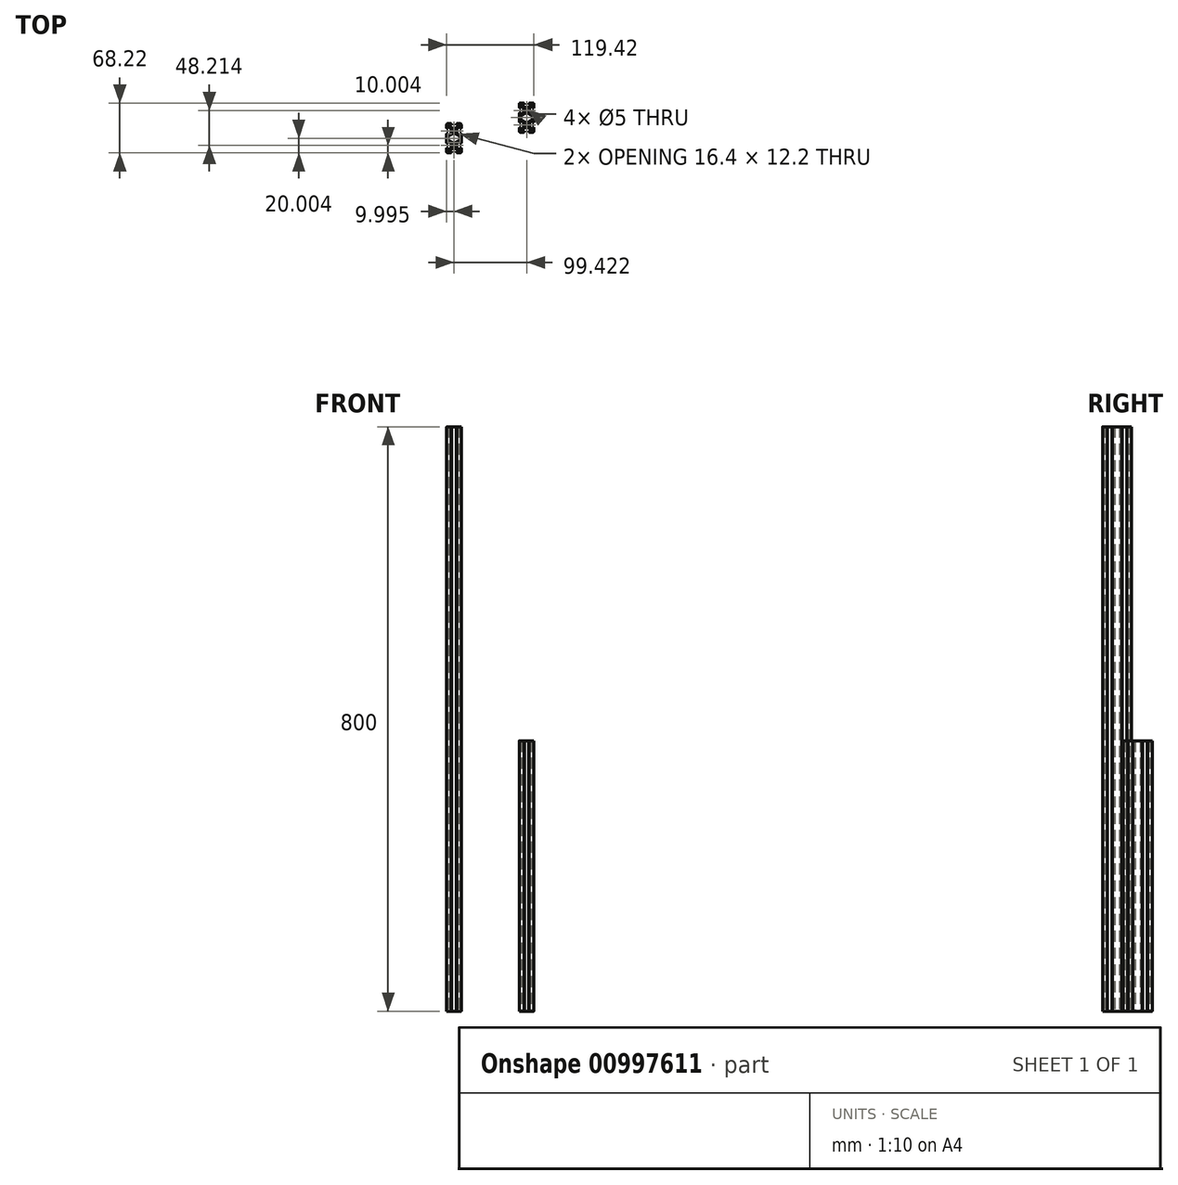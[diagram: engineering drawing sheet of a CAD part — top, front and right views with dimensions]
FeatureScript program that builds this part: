
annotation { "Feature Type Name" : "Feature", "Feature Type Description" : "" }
export const myFeature = defineFeature(function(context is Context, id is Id, definition is map)
    precondition{}
    {
        {
            var Q0;
            Q0=qCreatedBy(makeId("Top.planeOp"),FACE);
            var sketch = newSketch(context, id + "F0", { "sketchPlane" : qUnion([Q0])});
            skCircle(sketch, "E0", {"center": v(-160.4, -45.54) * mm, "radius": 2.5 * mm});
            skLineSegment(sketch, "E1.bottom", {"start": v(-151.9, -55.54) * mm, "end": v(-156.3, -55.54) * mm});
            skLineSegment(sketch, "E1.left", {"start": v(-150.4, -54.04) * mm, "end": v(-150.4, -49.14) * mm});
            skLineSegment(sketch, "E2.bottom", {"start": v(-158.38, -49.44) * mm, "end": v(-162.4, -49.44) * mm});
            skLineSegment(sketch, "E2.top", {"start": v(-158.38, -41.64) * mm, "end": v(-162.4, -41.64) * mm});
            skLineSegment(sketch, "E2.left", {"start": v(-156.5, -47.55) * mm, "end": v(-156.5, -43.52) * mm});
            skLineSegment(sketch, "E2.right", {"start": v(-164.3, -47.55) * mm, "end": v(-164.3, -43.52) * mm});
            skLineSegment(sketch, "E3.left", {"start": v(-150.4, -37.04) * mm, "end": v(-150.4, -40.04) * mm});
            skLineSegment(sketch, "E4", {"start": v(-155.9, -42.11) * mm, "end": v(-153.83, -40.04) * mm});
            skLineSegment(sketch, "E5.MirrorCS", {"start": v(-156.97, -41.05) * mm, "end": v(-154.9, -38.98) * mm});
            skLineSegment(sketch, "E6", {"start": v(-152.2, -40.04) * mm, "end": v(-152.2, -42.44) * mm});
            skLineSegment(sketch, "E7", {"start": v(-150.7, -41.94) * mm, "end": v(-150.4, -41.94) * mm});
            skLineSegment(sketch, "E8", {"start": v(-152.2, -42.44) * mm, "end": v(-150.9, -42.44) * mm});
            skLineSegment(sketch, "E9", {"start": v(-150.9, -42.14) * mm, "end": v(-150.9, -42.44) * mm});
            skPoint(sketch, "E10.visualSharp", {"position": v(-150.9, -41.94) * mm});
            skArc(sketch, "E10.filletArc", {"start": v(-150.7, -41.94) * mm, "mid": v(-150.84, -42) * mm, "end": v(-150.9, -42.14) * mm});
            skPoint(sketch, "E11.newPointA", {"position": v(-156.5, -42.7) * mm});
            skArc(sketch, "E11.filletArc", {"start": v(-155.9, -42.11) * mm, "mid": v(-156.34, -42.76) * mm, "end": v(-156.5, -43.52) * mm});
            skPoint(sketch, "E12.newPointA", {"position": v(-157.56, -41.64) * mm});
            skPoint(sketch, "E12.newPointB", {"position": v(-156.5, -41.64) * mm});
            skArc(sketch, "E12.filletArc", {"start": v(-158.38, -41.64) * mm, "mid": v(-157.62, -41.48) * mm, "end": v(-156.97, -41.05) * mm});
            skLineSegment(sketch, "E13.trimOffspring", {"start": v(-152.2, -40.04) * mm, "end": v(-153.83, -40.04) * mm});
            skLineSegment(sketch, "E14.MirrorCS", {"start": v(-150.7, -49.14) * mm, "end": v(-150.4, -49.14) * mm});
            skArc(sketch, "E15.MirrorCS", {"start": v(-150.7, -49.14) * mm, "mid": v(-150.84, -49.08) * mm, "end": v(-150.9, -48.94) * mm});
            skLineSegment(sketch, "E16.MirrorCS", {"start": v(-150.9, -48.94) * mm, "end": v(-150.9, -48.64) * mm});
            skArc(sketch, "E17.MirrorCS", {"start": v(-155.9, -48.96) * mm, "mid": v(-156.34, -48.31) * mm, "end": v(-156.5, -47.55) * mm});
            skLineSegment(sketch, "E18.MirrorCS", {"start": v(-152.2, -51.04) * mm, "end": v(-153.83, -51.04) * mm});
            skLineSegment(sketch, "E19.MirrorCS", {"start": v(-152.2, -48.64) * mm, "end": v(-150.9, -48.64) * mm});
            skLineSegment(sketch, "E20.MirrorCS", {"start": v(-151.9, -55.54) * mm, "end": v(-154.9, -55.54) * mm});
            skPoint(sketch, "E21.MirrorP", {"position": v(-150.9, -49.14) * mm});
            skLineSegment(sketch, "E22.MirrorCS", {"start": v(-157.3, -53.74) * mm, "end": v(-157.3, -55.04) * mm});
            skLineSegment(sketch, "E23.MirrorCS", {"start": v(-154.9, -53.74) * mm, "end": v(-157.3, -53.74) * mm});
            skLineSegment(sketch, "E24.MirrorCS", {"start": v(-152.2, -51.04) * mm, "end": v(-152.2, -48.64) * mm});
            skLineSegment(sketch, "E25.MirrorCS", {"start": v(-150.4, -54.04) * mm, "end": v(-150.4, -51.04) * mm});
            skLineSegment(sketch, "E26.MirrorCS", {"start": v(-155.9, -48.96) * mm, "end": v(-153.83, -51.04) * mm});
            skPoint(sketch, "E27.MirrorP", {"position": v(-156.5, -48.38) * mm});
            skPoint(sketch, "E28.MirrorP", {"position": v(-150.4, -55.54) * mm});
            skPoint(sketch, "E29.MirrorP", {"position": v(-156.5, -49.44) * mm});
            skLineSegment(sketch, "E30.MirrorCS", {"start": v(-156.97, -50.02) * mm, "end": v(-154.9, -52.1) * mm});
            skPoint(sketch, "E31.MirrorP", {"position": v(-157.56, -49.44) * mm});
            skArc(sketch, "E32.MirrorCS", {"start": v(-150.4, -54.04) * mm, "mid": v(-150.83, -55.1) * mm, "end": v(-151.9, -55.54) * mm});
            skLineSegment(sketch, "E33.MirrorCS", {"start": v(-154.9, -53.74) * mm, "end": v(-154.9, -52.1) * mm});
            skArc(sketch, "E34.MirrorCS", {"start": v(-158.38, -49.44) * mm, "mid": v(-157.62, -49.59) * mm, "end": v(-156.97, -50.02) * mm});
            skLineSegment(sketch, "E35.trimOffspring", {"start": v(-150.4, -41.94) * mm, "end": v(-150.4, -37.04) * mm});
            skLineSegment(sketch, "E36.MirrorCS", {"start": v(-156.8, -55.24) * mm, "end": v(-156.8, -55.54) * mm});
            skLineSegment(sketch, "E37.MirrorCS", {"start": v(-157, -55.04) * mm, "end": v(-157.3, -55.04) * mm});
            skLineSegment(sketch, "E38.MirrorCS", {"start": v(-156.3, -55.54) * mm, "end": v(-156.8, -55.54) * mm});
            skArc(sketch, "E39.MirrorCS", {"start": v(-156.8, -55.24) * mm, "mid": v(-156.85, -55.1) * mm, "end": v(-157, -55.04) * mm});
            skArc(sketch, "E40.MirrorCS", {"start": v(-170.1, -49.14) * mm, "mid": v(-169.95, -49.08) * mm, "end": v(-169.9, -48.94) * mm});
            skLineSegment(sketch, "E41.MirrorCS", {"start": v(-170.1, -41.94) * mm, "end": v(-170.4, -41.94) * mm});
            skLineSegment(sketch, "E42.MirrorCS", {"start": v(-169.9, -48.94) * mm, "end": v(-169.9, -48.64) * mm});
            skArc(sketch, "E43.MirrorCS", {"start": v(-170.1, -41.94) * mm, "mid": v(-169.95, -42) * mm, "end": v(-169.9, -42.14) * mm});
            skLineSegment(sketch, "E44.MirrorCS", {"start": v(-169.9, -42.14) * mm, "end": v(-169.9, -42.44) * mm});
            skLineSegment(sketch, "E45.MirrorCS", {"start": v(-170.1, -49.14) * mm, "end": v(-170.4, -49.14) * mm});
            skArc(sketch, "E46.MirrorCS", {"start": v(-170.4, -54.04) * mm, "mid": v(-169.96, -55.1) * mm, "end": v(-168.9, -55.54) * mm});
            skArc(sketch, "E47.MirrorCS", {"start": v(-164.88, -42.11) * mm, "mid": v(-164.45, -42.76) * mm, "end": v(-164.3, -43.52) * mm});
            skLineSegment(sketch, "E48.MirrorCS", {"start": v(-163.8, -55.04) * mm, "end": v(-163.5, -55.04) * mm});
            skLineSegment(sketch, "E49.MirrorCS", {"start": v(-162.4, -41.64) * mm, "end": v(-158.38, -41.64) * mm});
            skLineSegment(sketch, "E50.MirrorCS", {"start": v(-168.6, -48.64) * mm, "end": v(-169.9, -48.64) * mm});
            skLineSegment(sketch, "E51.MirrorCS", {"start": v(-168.6, -42.44) * mm, "end": v(-169.9, -42.44) * mm});
            skArc(sketch, "E52.MirrorCS", {"start": v(-164.88, -48.96) * mm, "mid": v(-164.45, -48.31) * mm, "end": v(-164.3, -47.55) * mm});
            skArc(sketch, "E53.MirrorCS", {"start": v(-164, -55.24) * mm, "mid": v(-163.94, -55.1) * mm, "end": v(-163.8, -55.04) * mm});
            skLineSegment(sketch, "E54.MirrorCS", {"start": v(-164, -55.24) * mm, "end": v(-164, -55.54) * mm});
            skLineSegment(sketch, "E55.MirrorCS", {"start": v(-162.4, -49.44) * mm, "end": v(-158.38, -49.44) * mm});
            skLineSegment(sketch, "E56.MirrorCS", {"start": v(-164.5, -55.54) * mm, "end": v(-164, -55.54) * mm});
            skLineSegment(sketch, "E57.MirrorCS", {"start": v(-163.5, -53.74) * mm, "end": v(-163.5, -55.04) * mm});
            skArc(sketch, "E58.MirrorCS", {"start": v(-162.4, -41.64) * mm, "mid": v(-163.17, -41.48) * mm, "end": v(-163.82, -41.05) * mm});
            skPoint(sketch, "E59.MirrorP", {"position": v(-170.4, -55.54) * mm});
            skLineSegment(sketch, "E60.MirrorCS", {"start": v(-168.9, -55.54) * mm, "end": v(-164.5, -55.54) * mm});
            skPoint(sketch, "E61.MirrorP", {"position": v(-164.3, -49.44) * mm});
            skArc(sketch, "E62.MirrorCS", {"start": v(-162.4, -49.44) * mm, "mid": v(-163.17, -49.59) * mm, "end": v(-163.82, -50.02) * mm});
            skPoint(sketch, "E63.MirrorP", {"position": v(-164.3, -48.38) * mm});
            skLineSegment(sketch, "E64.MirrorCS", {"start": v(-163.82, -41.05) * mm, "end": v(-165.9, -38.98) * mm});
            skPoint(sketch, "E65.MirrorP", {"position": v(-164.3, -42.7) * mm});
            skLineSegment(sketch, "E66.MirrorCS", {"start": v(-168.6, -51.04) * mm, "end": v(-168.6, -48.64) * mm});
            skLineSegment(sketch, "E67.MirrorCS", {"start": v(-164.88, -48.96) * mm, "end": v(-166.96, -51.04) * mm});
            skLineSegment(sketch, "E68.MirrorCS", {"start": v(-165.9, -53.74) * mm, "end": v(-163.5, -53.74) * mm});
            skLineSegment(sketch, "E69.MirrorCS", {"start": v(-168.6, -51.04) * mm, "end": v(-166.96, -51.04) * mm});
            skLineSegment(sketch, "E70.MirrorCS", {"start": v(-170.4, -54.04) * mm, "end": v(-170.4, -51.04) * mm});
            skLineSegment(sketch, "E71.MirrorCS", {"start": v(-170.4, -41.94) * mm, "end": v(-170.4, -37.04) * mm});
            skLineSegment(sketch, "E72.MirrorCS", {"start": v(-163.82, -50.02) * mm, "end": v(-165.9, -52.1) * mm});
            skPoint(sketch, "E73.MirrorP", {"position": v(-163.23, -49.44) * mm});
            skLineSegment(sketch, "E74.MirrorCS", {"start": v(-168.6, -40.04) * mm, "end": v(-168.6, -42.44) * mm});
            skLineSegment(sketch, "E75.MirrorCS", {"start": v(-170.4, -37.04) * mm, "end": v(-170.4, -40.04) * mm});
            skPoint(sketch, "E76.MirrorP", {"position": v(-169.9, -49.14) * mm});
            skPoint(sketch, "E77.MirrorP", {"position": v(-170.4, -35.54) * mm});
            skPoint(sketch, "E78.MirrorP", {"position": v(-169.9, -41.94) * mm});
            skLineSegment(sketch, "E79.MirrorCS", {"start": v(-164.88, -42.11) * mm, "end": v(-166.96, -40.04) * mm});
            skLineSegment(sketch, "E80.MirrorCS", {"start": v(-168.6, -40.04) * mm, "end": v(-166.96, -40.04) * mm});
            skLineSegment(sketch, "E81.MirrorCS", {"start": v(-170.4, -54.04) * mm, "end": v(-170.4, -49.14) * mm});
            skLineSegment(sketch, "E82.MirrorCS", {"start": v(-168.9, -55.54) * mm, "end": v(-165.9, -55.54) * mm});
            skPoint(sketch, "E83.MirrorP", {"position": v(-164.3, -41.64) * mm});
            skPoint(sketch, "E84.MirrorP", {"position": v(-163.23, -41.64) * mm});
            skLineSegment(sketch, "E85.MirrorCS", {"start": v(-165.9, -53.74) * mm, "end": v(-165.9, -52.1) * mm});
            skLineSegment(sketch, "E86", {"start": v(-168.6, -38.98) * mm, "end": v(-168.6, -35.54) * mm});
            skLineSegment(sketch, "E87", {"start": v(-170.4, -37.04) * mm, "end": v(-170.4, -35.54) * mm});
            skLineSegment(sketch, "E88", {"start": v(-150.4, -35.54) * mm, "end": v(-150.4, -37.04) * mm});
            skLineSegment(sketch, "E89", {"start": v(-152.2, -38.98) * mm, "end": v(-152.2, -35.54) * mm});
            skLineSegment(sketch, "E90", {"start": v(-154.9, -38.98) * mm, "end": v(-152.2, -38.98) * mm});
            skLineSegment(sketch, "E91", {"start": v(-165.9, -38.98) * mm, "end": v(-168.6, -38.98) * mm});
            skLineSegment(sketch, "E92.MirrorCS", {"start": v(-150.7, -21.94) * mm, "end": v(-150.4, -21.94) * mm});
            skLineSegment(sketch, "E93.MirrorCS", {"start": v(-150.9, -22.14) * mm, "end": v(-150.9, -22.44) * mm});
            skArc(sketch, "E94.MirrorCS", {"start": v(-150.7, -21.94) * mm, "mid": v(-150.84, -22) * mm, "end": v(-150.9, -22.14) * mm});
            skArc(sketch, "E95.MirrorCS", {"start": v(-150.7, -29.14) * mm, "mid": v(-150.84, -29.08) * mm, "end": v(-150.9, -28.94) * mm});
            skLineSegment(sketch, "E96.MirrorCS", {"start": v(-150.9, -28.94) * mm, "end": v(-150.9, -28.64) * mm});
            skLineSegment(sketch, "E97.MirrorCS", {"start": v(-169.9, -22.14) * mm, "end": v(-169.9, -22.44) * mm});
            skLineSegment(sketch, "E98.MirrorCS", {"start": v(-150.7, -29.14) * mm, "end": v(-150.4, -29.14) * mm});
            skArc(sketch, "E99.MirrorCS", {"start": v(-170.1, -21.94) * mm, "mid": v(-169.95, -22) * mm, "end": v(-169.9, -22.14) * mm});
            skLineSegment(sketch, "E100.MirrorCS", {"start": v(-170.1, -21.94) * mm, "end": v(-170.4, -21.94) * mm});
            skLineSegment(sketch, "E101.MirrorCS", {"start": v(-169.9, -28.94) * mm, "end": v(-169.9, -28.64) * mm});
            skArc(sketch, "E102.MirrorCS", {"start": v(-170.1, -29.14) * mm, "mid": v(-169.95, -29.08) * mm, "end": v(-169.9, -28.94) * mm});
            skLineSegment(sketch, "E103.MirrorCS", {"start": v(-170.1, -29.14) * mm, "end": v(-170.4, -29.14) * mm});
            skArc(sketch, "E104.MirrorCS", {"start": v(-158.38, -21.64) * mm, "mid": v(-157.62, -21.48) * mm, "end": v(-156.97, -21.05) * mm});
            skLineSegment(sketch, "E105.MirrorCS", {"start": v(-156.8, -15.84) * mm, "end": v(-156.8, -15.54) * mm});
            skArc(sketch, "E106.MirrorCS", {"start": v(-158.38, -29.44) * mm, "mid": v(-157.62, -29.59) * mm, "end": v(-156.97, -30.02) * mm});
            skLineSegment(sketch, "E107.MirrorCS", {"start": v(-152.2, -31.04) * mm, "end": v(-153.83, -31.04) * mm});
            skLineSegment(sketch, "E108.MirrorCS", {"start": v(-163.8, -16.04) * mm, "end": v(-163.5, -16.04) * mm});
            skLineSegment(sketch, "E109.MirrorCS", {"start": v(-168.6, -20.04) * mm, "end": v(-166.96, -20.04) * mm});
            skArc(sketch, "E110.MirrorCS", {"start": v(-170.4, -17.04) * mm, "mid": v(-169.96, -15.98) * mm, "end": v(-168.9, -15.54) * mm});
            skLineSegment(sketch, "E111.MirrorCS", {"start": v(-152.2, -28.64) * mm, "end": v(-150.9, -28.64) * mm});
            skLineSegment(sketch, "E112.MirrorCS", {"start": v(-164.5, -15.54) * mm, "end": v(-164, -15.54) * mm});
            skArc(sketch, "E113.MirrorCS", {"start": v(-164.88, -22.11) * mm, "mid": v(-164.45, -22.76) * mm, "end": v(-164.3, -23.52) * mm});
            skArc(sketch, "E114.MirrorCS", {"start": v(-150.4, -17.04) * mm, "mid": v(-150.83, -15.98) * mm, "end": v(-151.9, -15.54) * mm});
            skArc(sketch, "E115.MirrorCS", {"start": v(-162.4, -29.44) * mm, "mid": v(-163.17, -29.59) * mm, "end": v(-163.82, -30.02) * mm});
            skLineSegment(sketch, "E116.MirrorCS", {"start": v(-168.6, -22.44) * mm, "end": v(-169.9, -22.44) * mm});
            skLineSegment(sketch, "E117.MirrorCS", {"start": v(-164, -15.84) * mm, "end": v(-164, -15.54) * mm});
            skLineSegment(sketch, "E118.MirrorCS", {"start": v(-157.3, -17.34) * mm, "end": v(-157.3, -16.04) * mm});
            skLineSegment(sketch, "E119.MirrorCS", {"start": v(-156.3, -15.54) * mm, "end": v(-156.8, -15.54) * mm});
            skLineSegment(sketch, "E120.MirrorCS", {"start": v(-163.5, -17.34) * mm, "end": v(-163.5, -16.04) * mm});
            skArc(sketch, "E121.MirrorCS", {"start": v(-155.9, -28.96) * mm, "mid": v(-156.34, -28.31) * mm, "end": v(-156.5, -27.55) * mm});
            skArc(sketch, "E122.MirrorCS", {"start": v(-164.88, -28.96) * mm, "mid": v(-164.45, -28.31) * mm, "end": v(-164.3, -27.55) * mm});
            skLineSegment(sketch, "E123.MirrorCS", {"start": v(-152.2, -22.44) * mm, "end": v(-150.9, -22.44) * mm});
            skLineSegment(sketch, "E124.MirrorCS", {"start": v(-152.2, -20.04) * mm, "end": v(-153.83, -20.04) * mm});
            skArc(sketch, "E125.MirrorCS", {"start": v(-164, -15.84) * mm, "mid": v(-163.94, -15.98) * mm, "end": v(-163.8, -16.04) * mm});
            skLineSegment(sketch, "E126.MirrorCS", {"start": v(-157, -16.04) * mm, "end": v(-157.3, -16.04) * mm});
            skLineSegment(sketch, "E127.MirrorCS", {"start": v(-168.6, -31.04) * mm, "end": v(-166.96, -31.04) * mm});
            skLineSegment(sketch, "E128.MirrorCS", {"start": v(-168.6, -28.64) * mm, "end": v(-169.9, -28.64) * mm});
            skLineSegment(sketch, "E129.MirrorCS", {"start": v(-154.9, -17.34) * mm, "end": v(-154.9, -18.98) * mm});
            skLineSegment(sketch, "E130.MirrorCS", {"start": v(-165.9, -17.34) * mm, "end": v(-165.9, -18.98) * mm});
            skArc(sketch, "E131.MirrorCS", {"start": v(-162.4, -21.64) * mm, "mid": v(-163.17, -21.48) * mm, "end": v(-163.82, -21.05) * mm});
            skArc(sketch, "E132.MirrorCS", {"start": v(-155.9, -22.11) * mm, "mid": v(-156.34, -22.76) * mm, "end": v(-156.5, -23.52) * mm});
            skArc(sketch, "E133.MirrorCS", {"start": v(-156.8, -15.84) * mm, "mid": v(-156.85, -15.98) * mm, "end": v(-157, -16.04) * mm});
            skPoint(sketch, "E134.MirrorP", {"position": v(-160.4, -25.54) * mm});
            skLineSegment(sketch, "E135.MirrorCS", {"start": v(-164.3, -23.52) * mm, "end": v(-164.3, -27.55) * mm});
            skPoint(sketch, "E136.MirrorP", {"position": v(-164.3, -21.64) * mm});
            skLineSegment(sketch, "E137.MirrorCS", {"start": v(-151.9, -15.54) * mm, "end": v(-154.9, -15.54) * mm});
            skLineSegment(sketch, "E138.MirrorCS", {"start": v(-158.38, -29.44) * mm, "end": v(-162.4, -29.44) * mm});
            skLineSegment(sketch, "E139.MirrorCS", {"start": v(-170.4, -17.04) * mm, "end": v(-170.4, -21.94) * mm});
            skLineSegment(sketch, "E140.MirrorCS", {"start": v(-150.4, -34.04) * mm, "end": v(-150.4, -31.04) * mm});
            skPoint(sketch, "E141.MirrorP", {"position": v(-156.5, -21.64) * mm});
            skLineSegment(sketch, "E142.MirrorCS", {"start": v(-168.9, -15.54) * mm, "end": v(-164.5, -15.54) * mm});
            skLineSegment(sketch, "E143.MirrorCS", {"start": v(-150.4, -17.04) * mm, "end": v(-150.4, -20.04) * mm});
            skLineSegment(sketch, "E144.MirrorCS", {"start": v(-158.38, -21.64) * mm, "end": v(-162.4, -21.64) * mm});
            skPoint(sketch, "E145.MirrorP", {"position": v(-170.4, -15.54) * mm});
            skLineSegment(sketch, "E146.MirrorCS", {"start": v(-170.4, -34.04) * mm, "end": v(-170.4, -31.04) * mm});
            skCircle(sketch, "E147.MirrorC", {"center": v(-160.4, -25.54) * mm, "radius": 2.5 * mm});
            skPoint(sketch, "E148.MirrorP", {"position": v(-150.4, -15.54) * mm});
            skPoint(sketch, "E149.MirrorP", {"position": v(-169.9, -21.94) * mm});
            skLineSegment(sketch, "E150.MirrorCS", {"start": v(-152.2, -20.04) * mm, "end": v(-152.2, -22.44) * mm});
            skPoint(sketch, "E151.MirrorP", {"position": v(-169.9, -29.14) * mm});
            skPoint(sketch, "E152.MirrorP", {"position": v(-157.56, -21.64) * mm});
            skLineSegment(sketch, "E153.MirrorCS", {"start": v(-163.82, -21.05) * mm, "end": v(-165.9, -18.98) * mm});
            skLineSegment(sketch, "E154.MirrorCS", {"start": v(-165.9, -17.34) * mm, "end": v(-163.5, -17.34) * mm});
            skPoint(sketch, "E155.MirrorP", {"position": v(-156.5, -28.38) * mm});
            skLineSegment(sketch, "E156.MirrorCS", {"start": v(-170.4, -17.04) * mm, "end": v(-170.4, -20.04) * mm});
            skPoint(sketch, "E157.MirrorP", {"position": v(-150.9, -29.14) * mm});
            skLineSegment(sketch, "E158.MirrorCS", {"start": v(-154.9, -32.1) * mm, "end": v(-152.2, -32.1) * mm});
            skLineSegment(sketch, "E159.MirrorCS", {"start": v(-155.9, -22.11) * mm, "end": v(-153.83, -20.04) * mm});
            skLineSegment(sketch, "E160.MirrorCS", {"start": v(-165.9, -32.1) * mm, "end": v(-168.6, -32.1) * mm});
            skLineSegment(sketch, "E161.MirrorCS", {"start": v(-154.9, -17.34) * mm, "end": v(-157.3, -17.34) * mm});
            skLineSegment(sketch, "E162.MirrorCS", {"start": v(-168.6, -20.04) * mm, "end": v(-168.6, -22.44) * mm});
            skPoint(sketch, "E163.MirrorP", {"position": v(-164.3, -22.7) * mm});
            skPoint(sketch, "E164.MirrorP", {"position": v(-156.5, -29.44) * mm});
            skLineSegment(sketch, "E165.MirrorCS", {"start": v(-162.4, -21.64) * mm, "end": v(-158.38, -21.64) * mm});
            skLineSegment(sketch, "E166.MirrorCS", {"start": v(-168.9, -15.54) * mm, "end": v(-165.9, -15.54) * mm});
            skPoint(sketch, "E167.MirrorP", {"position": v(-163.23, -29.44) * mm});
            skLineSegment(sketch, "E168.MirrorCS", {"start": v(-162.4, -29.44) * mm, "end": v(-158.38, -29.44) * mm});
            skPoint(sketch, "E169.MirrorP", {"position": v(-164.3, -28.38) * mm});
            skLineSegment(sketch, "E170.MirrorCS", {"start": v(-150.4, -17.04) * mm, "end": v(-150.4, -21.94) * mm});
            skPoint(sketch, "E171.MirrorP", {"position": v(-156.5, -22.7) * mm});
            skLineSegment(sketch, "E172.MirrorCS", {"start": v(-164.88, -22.11) * mm, "end": v(-166.96, -20.04) * mm});
            skPoint(sketch, "E173.MirrorP", {"position": v(-163.23, -21.64) * mm});
            skLineSegment(sketch, "E174.MirrorCS", {"start": v(-155.9, -28.96) * mm, "end": v(-153.83, -31.04) * mm});
            skLineSegment(sketch, "E175.MirrorCS", {"start": v(-156.97, -21.05) * mm, "end": v(-154.9, -18.98) * mm});
            skLineSegment(sketch, "E176.MirrorCS", {"start": v(-170.4, -29.14) * mm, "end": v(-170.4, -34.04) * mm});
            skPoint(sketch, "E177.MirrorP", {"position": v(-164.3, -29.44) * mm});
            skLineSegment(sketch, "E178.MirrorCS", {"start": v(-156.97, -30.02) * mm, "end": v(-154.9, -32.1) * mm});
            skLineSegment(sketch, "E179.MirrorCS", {"start": v(-168.6, -31.04) * mm, "end": v(-168.6, -28.64) * mm});
            skPoint(sketch, "E180.MirrorP", {"position": v(-157.56, -29.44) * mm});
            skLineSegment(sketch, "E181.MirrorCS", {"start": v(-163.82, -30.02) * mm, "end": v(-165.9, -32.1) * mm});
            skLineSegment(sketch, "E182.MirrorCS", {"start": v(-152.2, -31.04) * mm, "end": v(-152.2, -28.64) * mm});
            skPoint(sketch, "E183.MirrorP", {"position": v(-150.9, -21.94) * mm});
            skLineSegment(sketch, "E184.MirrorCS", {"start": v(-150.4, -29.14) * mm, "end": v(-150.4, -34.04) * mm});
            skLineSegment(sketch, "E185.MirrorCS", {"start": v(-164.88, -28.96) * mm, "end": v(-166.96, -31.04) * mm});
            skLineSegment(sketch, "E186.MirrorCS", {"start": v(-156.5, -23.52) * mm, "end": v(-156.5, -27.55) * mm});
            skLineSegment(sketch, "E187.MirrorCS", {"start": v(-151.9, -15.54) * mm, "end": v(-156.3, -15.54) * mm});
            skLineSegment(sketch, "E188.MirrorCS", {"start": v(-152.2, -32.1) * mm, "end": v(-152.2, -35.54) * mm});
            skLineSegment(sketch, "E189.MirrorCS", {"start": v(-150.4, -35.54) * mm, "end": v(-150.4, -34.04) * mm});
            skLineSegment(sketch, "E190.MirrorCS", {"start": v(-168.6, -32.1) * mm, "end": v(-168.6, -35.54) * mm});
            skLineSegment(sketch, "E191.MirrorCS", {"start": v(-170.4, -34.04) * mm, "end": v(-170.4, -35.54) * mm});
            skSolve(sketch);
        }
        {
            var Q0;
            Q0=makeQuery(id+"F0.imprint","IMPRINT",FACE,{"disambiguationData":[TD([[makeQuery(id+"F0.imprint","IMPRINT",EDGE,{"derivedFrom":sQuery(id+"F0.wireOp",EDGE,"E1.bottom")}),-1.0]])]});
            extrude(context, id + "F1", {"entities" : qUnion([Q0]), "depth" : 800 * mm, "offsetDistance" : 25 * mm});
        }
        {
            var Q0;
            Q0=qCreatedBy(makeId("Top.planeOp"),FACE);
            var sketch = newSketch(context, id + "F2", { "sketchPlane" : qUnion([Q0])});
            skCircle(sketch, "E192", {"center": v(-60.97, -17.32) * mm, "radius": 2.5 * mm});
            skLineSegment(sketch, "E193.bottom", {"start": v(-52.47, -27.32) * mm, "end": v(-56.87, -27.32) * mm});
            skLineSegment(sketch, "E193.left", {"start": v(-50.97, -25.82) * mm, "end": v(-50.97, -20.92) * mm});
            skLineSegment(sketch, "E194.bottom", {"start": v(-58.96, -21.22) * mm, "end": v(-62.98, -21.22) * mm});
            skLineSegment(sketch, "E194.top", {"start": v(-58.96, -13.42) * mm, "end": v(-62.98, -13.42) * mm});
            skLineSegment(sketch, "E194.left", {"start": v(-57.07, -19.33) * mm, "end": v(-57.07, -15.31) * mm});
            skLineSegment(sketch, "E194.right", {"start": v(-64.87, -19.33) * mm, "end": v(-64.87, -15.31) * mm});
            skLineSegment(sketch, "E195.left", {"start": v(-50.97, -8.82) * mm, "end": v(-50.97, -11.82) * mm});
            skLineSegment(sketch, "E196", {"start": v(-56.49, -13.9) * mm, "end": v(-54.41, -11.82) * mm});
            skLineSegment(sketch, "E197.MirrorCS", {"start": v(-57.55, -12.84) * mm, "end": v(-55.47, -10.76) * mm});
            skLineSegment(sketch, "E198", {"start": v(-52.77, -11.82) * mm, "end": v(-52.77, -14.22) * mm});
            skLineSegment(sketch, "E199", {"start": v(-51.27, -13.72) * mm, "end": v(-50.97, -13.72) * mm});
            skLineSegment(sketch, "E200", {"start": v(-52.77, -14.22) * mm, "end": v(-51.47, -14.22) * mm});
            skLineSegment(sketch, "E201", {"start": v(-51.47, -13.92) * mm, "end": v(-51.47, -14.22) * mm});
            skPoint(sketch, "E202.visualSharp", {"position": v(-51.47, -13.72) * mm});
            skArc(sketch, "E202.filletArc", {"start": v(-51.27, -13.72) * mm, "mid": v(-51.41, -13.78) * mm, "end": v(-51.47, -13.92) * mm});
            skPoint(sketch, "E203.newPointA", {"position": v(-57.07, -14.48) * mm});
            skArc(sketch, "E203.filletArc", {"start": v(-56.49, -13.9) * mm, "mid": v(-56.92, -14.55) * mm, "end": v(-57.07, -15.31) * mm});
            skPoint(sketch, "E204.newPointA", {"position": v(-58.13, -13.42) * mm});
            skPoint(sketch, "E204.newPointB", {"position": v(-57.07, -13.42) * mm});
            skArc(sketch, "E204.filletArc", {"start": v(-58.96, -13.42) * mm, "mid": v(-58.2, -13.27) * mm, "end": v(-57.55, -12.84) * mm});
            skLineSegment(sketch, "E205.trimOffspring", {"start": v(-52.77, -11.82) * mm, "end": v(-54.41, -11.82) * mm});
            skLineSegment(sketch, "E206.MirrorCS", {"start": v(-51.27, -20.92) * mm, "end": v(-50.97, -20.92) * mm});
            skArc(sketch, "E207.MirrorCS", {"start": v(-51.27, -20.92) * mm, "mid": v(-51.41, -20.86) * mm, "end": v(-51.47, -20.72) * mm});
            skLineSegment(sketch, "E208.MirrorCS", {"start": v(-51.47, -20.72) * mm, "end": v(-51.47, -20.42) * mm});
            skArc(sketch, "E209.MirrorCS", {"start": v(-56.49, -20.75) * mm, "mid": v(-56.92, -20.1) * mm, "end": v(-57.07, -19.33) * mm});
            skLineSegment(sketch, "E210.MirrorCS", {"start": v(-52.77, -22.82) * mm, "end": v(-54.41, -22.82) * mm});
            skLineSegment(sketch, "E211.MirrorCS", {"start": v(-52.77, -20.42) * mm, "end": v(-51.47, -20.42) * mm});
            skLineSegment(sketch, "E212.MirrorCS", {"start": v(-52.47, -27.32) * mm, "end": v(-55.47, -27.32) * mm});
            skPoint(sketch, "E213.MirrorP", {"position": v(-51.47, -20.92) * mm});
            skLineSegment(sketch, "E214.MirrorCS", {"start": v(-57.87, -25.52) * mm, "end": v(-57.87, -26.82) * mm});
            skLineSegment(sketch, "E215.MirrorCS", {"start": v(-55.47, -25.52) * mm, "end": v(-57.87, -25.52) * mm});
            skLineSegment(sketch, "E216.MirrorCS", {"start": v(-52.77, -22.82) * mm, "end": v(-52.77, -20.42) * mm});
            skLineSegment(sketch, "E217.MirrorCS", {"start": v(-50.97, -25.82) * mm, "end": v(-50.97, -22.82) * mm});
            skLineSegment(sketch, "E218.MirrorCS", {"start": v(-56.49, -20.75) * mm, "end": v(-54.41, -22.82) * mm});
            skPoint(sketch, "E219.MirrorP", {"position": v(-57.07, -20.16) * mm});
            skPoint(sketch, "E220.MirrorP", {"position": v(-50.97, -27.32) * mm});
            skPoint(sketch, "E221.MirrorP", {"position": v(-57.07, -21.22) * mm});
            skLineSegment(sketch, "E222.MirrorCS", {"start": v(-57.55, -21.8) * mm, "end": v(-55.47, -23.88) * mm});
            skPoint(sketch, "E223.MirrorP", {"position": v(-58.13, -21.22) * mm});
            skArc(sketch, "E224.MirrorCS", {"start": v(-50.97, -25.82) * mm, "mid": v(-51.41, -26.88) * mm, "end": v(-52.47, -27.32) * mm});
            skLineSegment(sketch, "E225.MirrorCS", {"start": v(-55.47, -25.52) * mm, "end": v(-55.47, -23.88) * mm});
            skArc(sketch, "E226.MirrorCS", {"start": v(-58.96, -21.22) * mm, "mid": v(-58.2, -21.37) * mm, "end": v(-57.55, -21.8) * mm});
            skLineSegment(sketch, "E227.trimOffspring", {"start": v(-50.97, -13.72) * mm, "end": v(-50.97, -8.82) * mm});
            skLineSegment(sketch, "E228.MirrorCS", {"start": v(-57.37, -27.02) * mm, "end": v(-57.37, -27.32) * mm});
            skLineSegment(sketch, "E229.MirrorCS", {"start": v(-57.57, -26.82) * mm, "end": v(-57.87, -26.82) * mm});
            skLineSegment(sketch, "E230.MirrorCS", {"start": v(-56.87, -27.32) * mm, "end": v(-57.37, -27.32) * mm});
            skArc(sketch, "E231.MirrorCS", {"start": v(-57.37, -27.02) * mm, "mid": v(-57.43, -26.88) * mm, "end": v(-57.57, -26.82) * mm});
            skArc(sketch, "E232.MirrorCS", {"start": v(-70.67, -20.92) * mm, "mid": v(-70.53, -20.86) * mm, "end": v(-70.47, -20.72) * mm});
            skLineSegment(sketch, "E233.MirrorCS", {"start": v(-70.67, -13.72) * mm, "end": v(-70.97, -13.72) * mm});
            skLineSegment(sketch, "E234.MirrorCS", {"start": v(-70.47, -20.72) * mm, "end": v(-70.47, -20.42) * mm});
            skArc(sketch, "E235.MirrorCS", {"start": v(-70.67, -13.72) * mm, "mid": v(-70.53, -13.78) * mm, "end": v(-70.47, -13.92) * mm});
            skLineSegment(sketch, "E236.MirrorCS", {"start": v(-70.47, -13.92) * mm, "end": v(-70.47, -14.22) * mm});
            skLineSegment(sketch, "E237.MirrorCS", {"start": v(-70.67, -20.92) * mm, "end": v(-70.97, -20.92) * mm});
            skArc(sketch, "E238.MirrorCS", {"start": v(-70.97, -25.82) * mm, "mid": v(-70.53, -26.88) * mm, "end": v(-69.47, -27.32) * mm});
            skArc(sketch, "E239.MirrorCS", {"start": v(-65.46, -13.9) * mm, "mid": v(-65.02, -14.55) * mm, "end": v(-64.87, -15.31) * mm});
            skLineSegment(sketch, "E240.MirrorCS", {"start": v(-64.37, -26.82) * mm, "end": v(-64.07, -26.82) * mm});
            skLineSegment(sketch, "E241.MirrorCS", {"start": v(-62.98, -13.42) * mm, "end": v(-58.96, -13.42) * mm});
            skLineSegment(sketch, "E242.MirrorCS", {"start": v(-69.17, -20.42) * mm, "end": v(-70.47, -20.42) * mm});
            skLineSegment(sketch, "E243.MirrorCS", {"start": v(-69.17, -14.22) * mm, "end": v(-70.47, -14.22) * mm});
            skArc(sketch, "E244.MirrorCS", {"start": v(-65.46, -20.75) * mm, "mid": v(-65.02, -20.1) * mm, "end": v(-64.87, -19.33) * mm});
            skArc(sketch, "E245.MirrorCS", {"start": v(-64.57, -27.02) * mm, "mid": v(-64.51, -26.88) * mm, "end": v(-64.37, -26.82) * mm});
            skLineSegment(sketch, "E246.MirrorCS", {"start": v(-64.57, -27.02) * mm, "end": v(-64.57, -27.32) * mm});
            skLineSegment(sketch, "E247.MirrorCS", {"start": v(-62.98, -21.22) * mm, "end": v(-58.96, -21.22) * mm});
            skLineSegment(sketch, "E248.MirrorCS", {"start": v(-65.07, -27.32) * mm, "end": v(-64.57, -27.32) * mm});
            skLineSegment(sketch, "E249.MirrorCS", {"start": v(-64.07, -25.52) * mm, "end": v(-64.07, -26.82) * mm});
            skArc(sketch, "E250.MirrorCS", {"start": v(-62.98, -13.42) * mm, "mid": v(-63.75, -13.27) * mm, "end": v(-64.4, -12.84) * mm});
            skPoint(sketch, "E251.MirrorP", {"position": v(-70.97, -27.32) * mm});
            skLineSegment(sketch, "E252.MirrorCS", {"start": v(-69.47, -27.32) * mm, "end": v(-65.07, -27.32) * mm});
            skPoint(sketch, "E253.MirrorP", {"position": v(-64.87, -21.22) * mm});
            skArc(sketch, "E254.MirrorCS", {"start": v(-62.98, -21.22) * mm, "mid": v(-63.75, -21.37) * mm, "end": v(-64.4, -21.8) * mm});
            skPoint(sketch, "E255.MirrorP", {"position": v(-64.87, -20.16) * mm});
            skLineSegment(sketch, "E256.MirrorCS", {"start": v(-64.4, -12.84) * mm, "end": v(-66.47, -10.76) * mm});
            skPoint(sketch, "E257.MirrorP", {"position": v(-64.87, -14.48) * mm});
            skLineSegment(sketch, "E258.MirrorCS", {"start": v(-69.17, -22.82) * mm, "end": v(-69.17, -20.42) * mm});
            skLineSegment(sketch, "E259.MirrorCS", {"start": v(-65.46, -20.75) * mm, "end": v(-67.53, -22.82) * mm});
            skLineSegment(sketch, "E260.MirrorCS", {"start": v(-66.47, -25.52) * mm, "end": v(-64.07, -25.52) * mm});
            skLineSegment(sketch, "E261.MirrorCS", {"start": v(-69.17, -22.82) * mm, "end": v(-67.53, -22.82) * mm});
            skLineSegment(sketch, "E262.MirrorCS", {"start": v(-70.97, -25.82) * mm, "end": v(-70.97, -22.82) * mm});
            skLineSegment(sketch, "E263.MirrorCS", {"start": v(-70.97, -13.72) * mm, "end": v(-70.97, -8.82) * mm});
            skLineSegment(sketch, "E264.MirrorCS", {"start": v(-64.4, -21.8) * mm, "end": v(-66.47, -23.88) * mm});
            skPoint(sketch, "E265.MirrorP", {"position": v(-63.81, -21.22) * mm});
            skLineSegment(sketch, "E266.MirrorCS", {"start": v(-69.17, -11.82) * mm, "end": v(-69.17, -14.22) * mm});
            skLineSegment(sketch, "E267.MirrorCS", {"start": v(-70.97, -8.82) * mm, "end": v(-70.97, -11.82) * mm});
            skPoint(sketch, "E268.MirrorP", {"position": v(-70.47, -20.92) * mm});
            skPoint(sketch, "E269.MirrorP", {"position": v(-70.97, -7.32) * mm});
            skPoint(sketch, "E270.MirrorP", {"position": v(-70.47, -13.72) * mm});
            skLineSegment(sketch, "E271.MirrorCS", {"start": v(-65.46, -13.9) * mm, "end": v(-67.53, -11.82) * mm});
            skLineSegment(sketch, "E272.MirrorCS", {"start": v(-69.17, -11.82) * mm, "end": v(-67.53, -11.82) * mm});
            skLineSegment(sketch, "E273.MirrorCS", {"start": v(-70.97, -25.82) * mm, "end": v(-70.97, -20.92) * mm});
            skLineSegment(sketch, "E274.MirrorCS", {"start": v(-69.47, -27.32) * mm, "end": v(-66.47, -27.32) * mm});
            skPoint(sketch, "E275.MirrorP", {"position": v(-64.87, -13.42) * mm});
            skPoint(sketch, "E276.MirrorP", {"position": v(-63.81, -13.42) * mm});
            skLineSegment(sketch, "E277.MirrorCS", {"start": v(-66.47, -25.52) * mm, "end": v(-66.47, -23.88) * mm});
            skLineSegment(sketch, "E278", {"start": v(-69.17, -10.76) * mm, "end": v(-69.17, -7.32) * mm});
            skLineSegment(sketch, "E279", {"start": v(-70.97, -8.82) * mm, "end": v(-70.97, -7.32) * mm});
            skLineSegment(sketch, "E280", {"start": v(-50.97, -7.32) * mm, "end": v(-50.97, -8.82) * mm});
            skLineSegment(sketch, "E281", {"start": v(-52.77, -10.76) * mm, "end": v(-52.77, -7.32) * mm});
            skLineSegment(sketch, "E282", {"start": v(-55.47, -10.76) * mm, "end": v(-52.77, -10.76) * mm});
            skLineSegment(sketch, "E283", {"start": v(-66.47, -10.76) * mm, "end": v(-69.17, -10.76) * mm});
            skLineSegment(sketch, "E284.MirrorCS", {"start": v(-51.27, 6.28) * mm, "end": v(-50.97, 6.28) * mm});
            skLineSegment(sketch, "E285.MirrorCS", {"start": v(-51.47, 6.08) * mm, "end": v(-51.47, 5.78) * mm});
            skArc(sketch, "E286.MirrorCS", {"start": v(-51.27, 6.28) * mm, "mid": v(-51.41, 6.22) * mm, "end": v(-51.47, 6.08) * mm});
            skArc(sketch, "E287.MirrorCS", {"start": v(-51.27, -0.92) * mm, "mid": v(-51.41, -0.86) * mm, "end": v(-51.47, -0.72) * mm});
            skLineSegment(sketch, "E288.MirrorCS", {"start": v(-51.47, -0.72) * mm, "end": v(-51.47, -0.42) * mm});
            skLineSegment(sketch, "E289.MirrorCS", {"start": v(-70.47, 6.08) * mm, "end": v(-70.47, 5.78) * mm});
            skLineSegment(sketch, "E290.MirrorCS", {"start": v(-51.27, -0.92) * mm, "end": v(-50.97, -0.92) * mm});
            skArc(sketch, "E291.MirrorCS", {"start": v(-70.67, 6.28) * mm, "mid": v(-70.53, 6.22) * mm, "end": v(-70.47, 6.08) * mm});
            skLineSegment(sketch, "E292.MirrorCS", {"start": v(-70.67, 6.28) * mm, "end": v(-70.97, 6.28) * mm});
            skLineSegment(sketch, "E293.MirrorCS", {"start": v(-70.47, -0.72) * mm, "end": v(-70.47, -0.42) * mm});
            skArc(sketch, "E294.MirrorCS", {"start": v(-70.67, -0.92) * mm, "mid": v(-70.53, -0.86) * mm, "end": v(-70.47, -0.72) * mm});
            skLineSegment(sketch, "E295.MirrorCS", {"start": v(-70.67, -0.92) * mm, "end": v(-70.97, -0.92) * mm});
            skArc(sketch, "E296.MirrorCS", {"start": v(-58.96, 6.58) * mm, "mid": v(-58.2, 6.73) * mm, "end": v(-57.55, 7.16) * mm});
            skLineSegment(sketch, "E297.MirrorCS", {"start": v(-57.37, 12.38) * mm, "end": v(-57.37, 12.68) * mm});
            skArc(sketch, "E298.MirrorCS", {"start": v(-58.96, -1.22) * mm, "mid": v(-58.2, -1.37) * mm, "end": v(-57.55, -1.8) * mm});
            skLineSegment(sketch, "E299.MirrorCS", {"start": v(-52.77, -2.82) * mm, "end": v(-54.41, -2.82) * mm});
            skLineSegment(sketch, "E300.MirrorCS", {"start": v(-64.37, 12.18) * mm, "end": v(-64.07, 12.18) * mm});
            skLineSegment(sketch, "E301.MirrorCS", {"start": v(-69.17, 8.18) * mm, "end": v(-67.53, 8.18) * mm});
            skArc(sketch, "E302.MirrorCS", {"start": v(-70.97, 11.18) * mm, "mid": v(-70.53, 12.24) * mm, "end": v(-69.47, 12.68) * mm});
            skLineSegment(sketch, "E303.MirrorCS", {"start": v(-52.77, -0.42) * mm, "end": v(-51.47, -0.42) * mm});
            skLineSegment(sketch, "E304.MirrorCS", {"start": v(-65.07, 12.68) * mm, "end": v(-64.57, 12.68) * mm});
            skArc(sketch, "E305.MirrorCS", {"start": v(-65.46, 6.1) * mm, "mid": v(-65.02, 5.45) * mm, "end": v(-64.87, 4.69) * mm});
            skArc(sketch, "E306.MirrorCS", {"start": v(-50.97, 11.18) * mm, "mid": v(-51.41, 12.24) * mm, "end": v(-52.47, 12.68) * mm});
            skArc(sketch, "E307.MirrorCS", {"start": v(-62.98, -1.22) * mm, "mid": v(-63.75, -1.37) * mm, "end": v(-64.4, -1.8) * mm});
            skLineSegment(sketch, "E308.MirrorCS", {"start": v(-69.17, 5.78) * mm, "end": v(-70.47, 5.78) * mm});
            skLineSegment(sketch, "E309.MirrorCS", {"start": v(-64.57, 12.38) * mm, "end": v(-64.57, 12.68) * mm});
            skLineSegment(sketch, "E310.MirrorCS", {"start": v(-57.87, 10.88) * mm, "end": v(-57.87, 12.18) * mm});
            skLineSegment(sketch, "E311.MirrorCS", {"start": v(-56.87, 12.68) * mm, "end": v(-57.37, 12.68) * mm});
            skLineSegment(sketch, "E312.MirrorCS", {"start": v(-64.07, 10.88) * mm, "end": v(-64.07, 12.18) * mm});
            skArc(sketch, "E313.MirrorCS", {"start": v(-56.49, -0.75) * mm, "mid": v(-56.92, -0.1) * mm, "end": v(-57.07, 0.67) * mm});
            skArc(sketch, "E314.MirrorCS", {"start": v(-65.46, -0.75) * mm, "mid": v(-65.02, -0.1) * mm, "end": v(-64.87, 0.67) * mm});
            skLineSegment(sketch, "E315.MirrorCS", {"start": v(-52.77, 5.78) * mm, "end": v(-51.47, 5.78) * mm});
            skLineSegment(sketch, "E316.MirrorCS", {"start": v(-52.77, 8.18) * mm, "end": v(-54.41, 8.18) * mm});
            skArc(sketch, "E317.MirrorCS", {"start": v(-64.57, 12.38) * mm, "mid": v(-64.51, 12.24) * mm, "end": v(-64.37, 12.18) * mm});
            skLineSegment(sketch, "E318.MirrorCS", {"start": v(-57.57, 12.18) * mm, "end": v(-57.87, 12.18) * mm});
            skLineSegment(sketch, "E319.MirrorCS", {"start": v(-69.17, -2.82) * mm, "end": v(-67.53, -2.82) * mm});
            skLineSegment(sketch, "E320.MirrorCS", {"start": v(-69.17, -0.42) * mm, "end": v(-70.47, -0.42) * mm});
            skLineSegment(sketch, "E321.MirrorCS", {"start": v(-55.47, 10.88) * mm, "end": v(-55.47, 9.24) * mm});
            skLineSegment(sketch, "E322.MirrorCS", {"start": v(-66.47, 10.88) * mm, "end": v(-66.47, 9.24) * mm});
            skArc(sketch, "E323.MirrorCS", {"start": v(-62.98, 6.58) * mm, "mid": v(-63.75, 6.73) * mm, "end": v(-64.4, 7.16) * mm});
            skArc(sketch, "E324.MirrorCS", {"start": v(-56.49, 6.1) * mm, "mid": v(-56.92, 5.45) * mm, "end": v(-57.07, 4.69) * mm});
            skArc(sketch, "E325.MirrorCS", {"start": v(-57.37, 12.38) * mm, "mid": v(-57.43, 12.24) * mm, "end": v(-57.57, 12.18) * mm});
            skPoint(sketch, "E326.MirrorP", {"position": v(-60.97, 2.68) * mm});
            skLineSegment(sketch, "E327.MirrorCS", {"start": v(-64.87, 4.69) * mm, "end": v(-64.87, 0.67) * mm});
            skPoint(sketch, "E328.MirrorP", {"position": v(-64.87, 6.58) * mm});
            skLineSegment(sketch, "E329.MirrorCS", {"start": v(-52.47, 12.68) * mm, "end": v(-55.47, 12.68) * mm});
            skLineSegment(sketch, "E330.MirrorCS", {"start": v(-58.96, -1.22) * mm, "end": v(-62.98, -1.22) * mm});
            skLineSegment(sketch, "E331.MirrorCS", {"start": v(-70.97, 11.18) * mm, "end": v(-70.97, 6.28) * mm});
            skLineSegment(sketch, "E332.MirrorCS", {"start": v(-50.97, -5.82) * mm, "end": v(-50.97, -2.82) * mm});
            skPoint(sketch, "E333.MirrorP", {"position": v(-57.07, 6.58) * mm});
            skLineSegment(sketch, "E334.MirrorCS", {"start": v(-69.47, 12.68) * mm, "end": v(-65.07, 12.68) * mm});
            skLineSegment(sketch, "E335.MirrorCS", {"start": v(-50.97, 11.18) * mm, "end": v(-50.97, 8.18) * mm});
            skLineSegment(sketch, "E336.MirrorCS", {"start": v(-58.96, 6.58) * mm, "end": v(-62.98, 6.58) * mm});
            skPoint(sketch, "E337.MirrorP", {"position": v(-70.97, 12.68) * mm});
            skLineSegment(sketch, "E338.MirrorCS", {"start": v(-70.97, -5.82) * mm, "end": v(-70.97, -2.82) * mm});
            skCircle(sketch, "E339.MirrorC", {"center": v(-60.97, 2.68) * mm, "radius": 2.5 * mm});
            skPoint(sketch, "E340.MirrorP", {"position": v(-50.97, 12.68) * mm});
            skPoint(sketch, "E341.MirrorP", {"position": v(-70.47, 6.28) * mm});
            skLineSegment(sketch, "E342.MirrorCS", {"start": v(-52.77, 8.18) * mm, "end": v(-52.77, 5.78) * mm});
            skPoint(sketch, "E343.MirrorP", {"position": v(-70.47, -0.92) * mm});
            skPoint(sketch, "E344.MirrorP", {"position": v(-58.13, 6.58) * mm});
            skLineSegment(sketch, "E345.MirrorCS", {"start": v(-64.4, 7.16) * mm, "end": v(-66.47, 9.24) * mm});
            skLineSegment(sketch, "E346.MirrorCS", {"start": v(-66.47, 10.88) * mm, "end": v(-64.07, 10.88) * mm});
            skPoint(sketch, "E347.MirrorP", {"position": v(-57.07, -0.16) * mm});
            skLineSegment(sketch, "E348.MirrorCS", {"start": v(-70.97, 11.18) * mm, "end": v(-70.97, 8.18) * mm});
            skPoint(sketch, "E349.MirrorP", {"position": v(-51.47, -0.92) * mm});
            skLineSegment(sketch, "E350.MirrorCS", {"start": v(-55.47, -3.88) * mm, "end": v(-52.77, -3.88) * mm});
            skLineSegment(sketch, "E351.MirrorCS", {"start": v(-56.49, 6.1) * mm, "end": v(-54.41, 8.18) * mm});
            skLineSegment(sketch, "E352.MirrorCS", {"start": v(-66.47, -3.88) * mm, "end": v(-69.17, -3.88) * mm});
            skLineSegment(sketch, "E353.MirrorCS", {"start": v(-55.47, 10.88) * mm, "end": v(-57.87, 10.88) * mm});
            skLineSegment(sketch, "E354.MirrorCS", {"start": v(-69.17, 8.18) * mm, "end": v(-69.17, 5.78) * mm});
            skPoint(sketch, "E355.MirrorP", {"position": v(-64.87, 5.52) * mm});
            skPoint(sketch, "E356.MirrorP", {"position": v(-57.07, -1.22) * mm});
            skLineSegment(sketch, "E357.MirrorCS", {"start": v(-62.98, 6.58) * mm, "end": v(-58.96, 6.58) * mm});
            skLineSegment(sketch, "E358.MirrorCS", {"start": v(-69.47, 12.68) * mm, "end": v(-66.47, 12.68) * mm});
            skPoint(sketch, "E359.MirrorP", {"position": v(-63.81, -1.22) * mm});
            skLineSegment(sketch, "E360.MirrorCS", {"start": v(-62.98, -1.22) * mm, "end": v(-58.96, -1.22) * mm});
            skPoint(sketch, "E361.MirrorP", {"position": v(-64.87, -0.16) * mm});
            skLineSegment(sketch, "E362.MirrorCS", {"start": v(-50.97, 11.18) * mm, "end": v(-50.97, 6.28) * mm});
            skPoint(sketch, "E363.MirrorP", {"position": v(-57.07, 5.52) * mm});
            skLineSegment(sketch, "E364.MirrorCS", {"start": v(-65.46, 6.1) * mm, "end": v(-67.53, 8.18) * mm});
            skPoint(sketch, "E365.MirrorP", {"position": v(-63.81, 6.58) * mm});
            skLineSegment(sketch, "E366.MirrorCS", {"start": v(-56.49, -0.75) * mm, "end": v(-54.41, -2.82) * mm});
            skLineSegment(sketch, "E367.MirrorCS", {"start": v(-57.55, 7.16) * mm, "end": v(-55.47, 9.24) * mm});
            skLineSegment(sketch, "E368.MirrorCS", {"start": v(-70.97, -0.92) * mm, "end": v(-70.97, -5.82) * mm});
            skPoint(sketch, "E369.MirrorP", {"position": v(-64.87, -1.22) * mm});
            skLineSegment(sketch, "E370.MirrorCS", {"start": v(-57.55, -1.8) * mm, "end": v(-55.47, -3.88) * mm});
            skLineSegment(sketch, "E371.MirrorCS", {"start": v(-69.17, -2.82) * mm, "end": v(-69.17, -0.42) * mm});
            skPoint(sketch, "E372.MirrorP", {"position": v(-58.13, -1.22) * mm});
            skLineSegment(sketch, "E373.MirrorCS", {"start": v(-64.4, -1.8) * mm, "end": v(-66.47, -3.88) * mm});
            skLineSegment(sketch, "E374.MirrorCS", {"start": v(-52.77, -2.82) * mm, "end": v(-52.77, -0.42) * mm});
            skPoint(sketch, "E375.MirrorP", {"position": v(-51.47, 6.28) * mm});
            skLineSegment(sketch, "E376.MirrorCS", {"start": v(-50.97, -0.92) * mm, "end": v(-50.97, -5.82) * mm});
            skLineSegment(sketch, "E377.MirrorCS", {"start": v(-65.46, -0.75) * mm, "end": v(-67.53, -2.82) * mm});
            skLineSegment(sketch, "E378.MirrorCS", {"start": v(-57.07, 4.69) * mm, "end": v(-57.07, 0.67) * mm});
            skLineSegment(sketch, "E379.MirrorCS", {"start": v(-52.47, 12.68) * mm, "end": v(-56.87, 12.68) * mm});
            skLineSegment(sketch, "E380.MirrorCS", {"start": v(-52.77, -3.88) * mm, "end": v(-52.77, -7.32) * mm});
            skLineSegment(sketch, "E381.MirrorCS", {"start": v(-50.97, -7.32) * mm, "end": v(-50.97, -5.82) * mm});
            skLineSegment(sketch, "E382.MirrorCS", {"start": v(-69.17, -3.88) * mm, "end": v(-69.17, -7.32) * mm});
            skLineSegment(sketch, "E383.MirrorCS", {"start": v(-70.97, -5.82) * mm, "end": v(-70.97, -7.32) * mm});
            skSolve(sketch);
        }
        {
            var Q0;
            Q0=makeQuery(id+"F2.imprint","IMPRINT",FACE,{"disambiguationData":[TD([[makeQuery(id+"F2.imprint","IMPRINT",EDGE,{"derivedFrom":sQuery(id+"F2.wireOp",EDGE,"E193.bottom")}),-1.0]])]});
            extrude(context, id + "F3", {"entities" : qUnion([Q0]), "depth" : 370 * mm, "offsetDistance" : 25 * mm});
        }
    });
